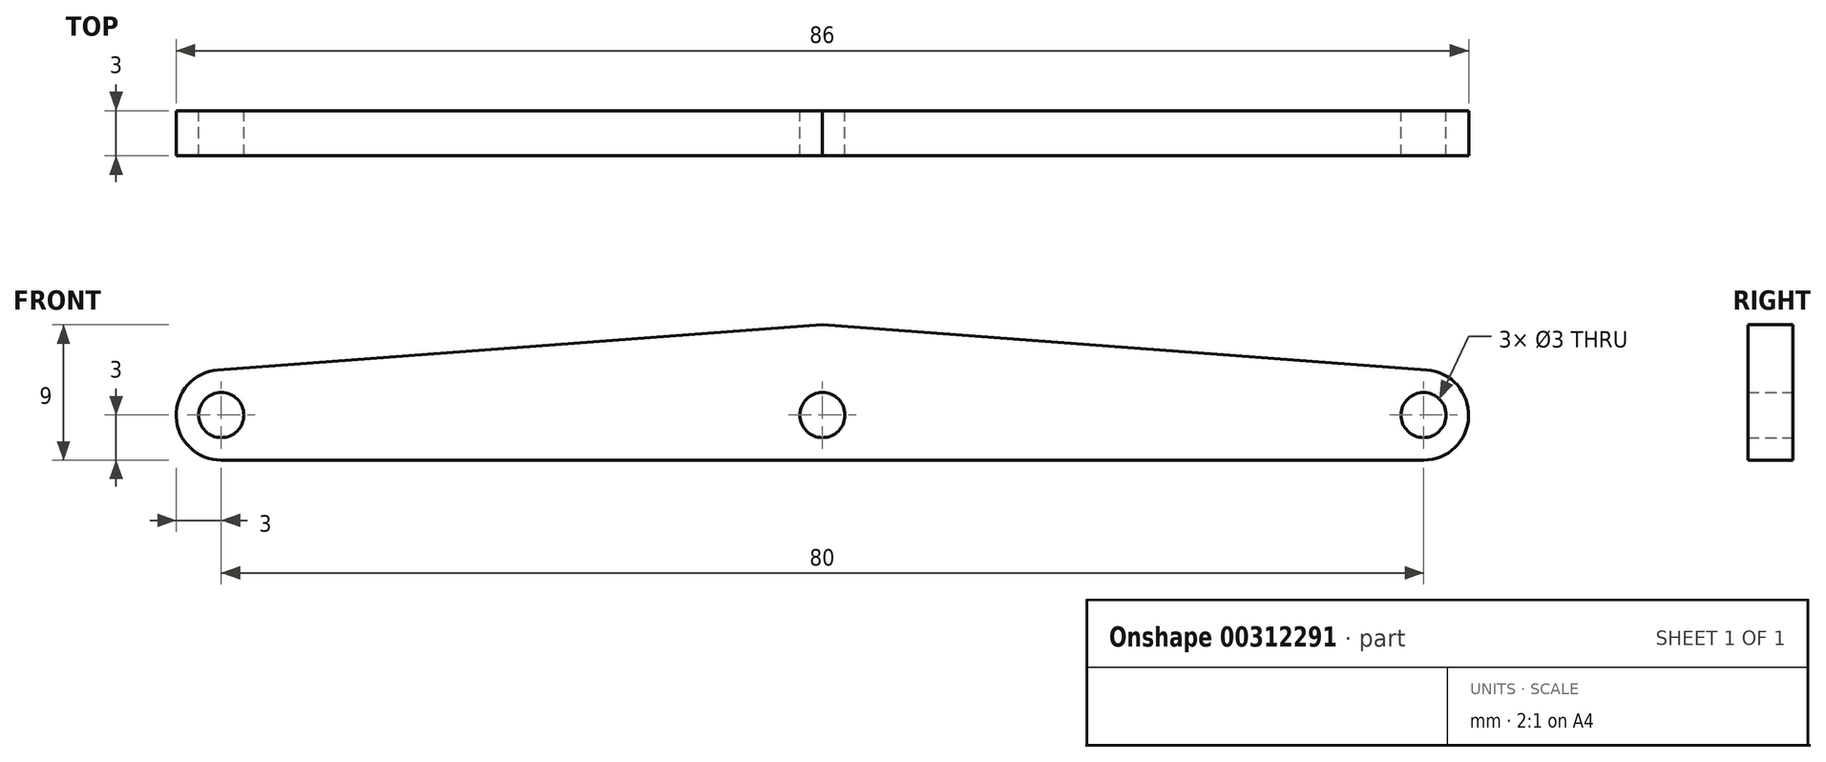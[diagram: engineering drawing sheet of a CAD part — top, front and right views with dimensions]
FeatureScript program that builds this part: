
annotation { "Feature Type Name" : "Feature", "Feature Type Description" : "" }
export const myFeature = defineFeature(function(context is Context, id is Id, definition is map)
    precondition{}
    {
        {
            var Q0;
            Q0=qCreatedBy(makeId("Front.planeOp"),FACE);
            var sketch = newSketch(context, id + "F0", { "sketchPlane" : qUnion([Q0])});
            skLineSegment(sketch, "E0", {"start": v(0, 0) * mm, "end": v(0, 12) * mm, "construction": true});
            skLineSegment(sketch, "E1", {"start": v(0, 0) * mm, "end": v(36.64, 0) * mm, "construction": true});
            skLineSegment(sketch, "E2", {"start": v(0, -3) * mm, "end": v(40, -3) * mm});
            skArc(sketch, "E3", {"start": v(40, -3) * mm, "mid": v(43, -0.11) * mm, "end": v(40.22, 3) * mm});
            skLineSegment(sketch, "E4", {"start": v(40.22, 3) * mm, "end": v(0, 6) * mm});
            skPoint(sketch, "E4.endSnap0", {"position": v(0, 6) * mm});
            skLineSegment(sketch, "E5.MirrorCS", {"start": v(-40.22, 3) * mm, "end": v(0, 6) * mm});
            skArc(sketch, "E6.MirrorCS", {"start": v(-40, -3) * mm, "mid": v(-43, -0.11) * mm, "end": v(-40.22, 3) * mm});
            skLineSegment(sketch, "E7.MirrorCS", {"start": v(0, -3) * mm, "end": v(-40, -3) * mm});
            skCircle(sketch, "E8", {"center": v(0, 0) * mm, "radius": 1.5 * mm});
            skCircle(sketch, "E9", {"center": v(-40, 0) * mm, "radius": 1.5 * mm});
            skCircle(sketch, "E10", {"center": v(40, 0) * mm, "radius": 1.5 * mm});
            skSolve(sketch);
        }
        {
            var Q0;
            Q0 = qSketchRegion(id + "F0", true);
            extrude(context, id + "F1", {"entities" : qUnion([Q0]), "depth" : 1.5 * mm, "hasSecondDirection" : true, "secondDirectionOppositeDirection" : true, "secondDirectionDepth" : 1.5 * mm});
        }
    });
